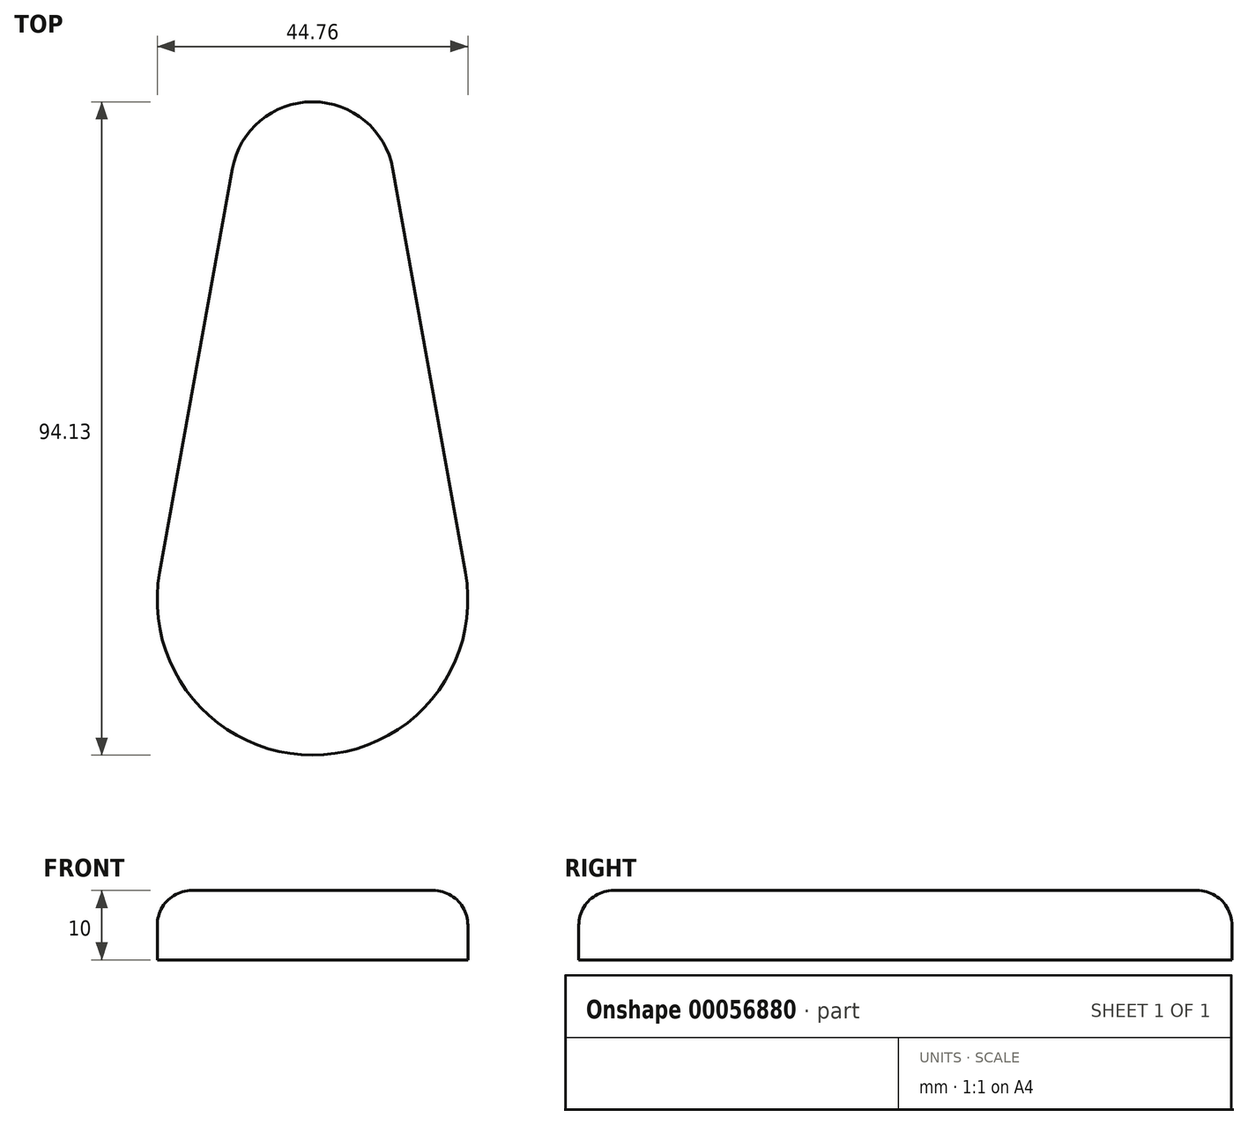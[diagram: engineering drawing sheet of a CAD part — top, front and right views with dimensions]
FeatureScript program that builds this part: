
annotation { "Feature Type Name" : "Feature", "Feature Type Description" : "" }
export const myFeature = defineFeature(function(context is Context, id is Id, definition is map)
    precondition{}
    {
        {
            var Q0;
            Q0=qCreatedBy(makeId("Top.planeOp"),FACE);
            var sketch = newSketch(context, id + "F0", { "sketchPlane" : qUnion([Q0])});
            skCircle(sketch, "E0", {"center": v(0, 0) * mm, "radius": 22.38 * mm});
            skCircle(sketch, "E1", {"center": v(0, 59.99) * mm, "radius": 11.76 * mm});
            skLineSegment(sketch, "E2", {"start": v(-11.57, 62.07) * mm, "end": v(-22.03, 3.96) * mm});
            skLineSegment(sketch, "E3", {"start": v(11.57, 62.07) * mm, "end": v(22.03, 3.96) * mm});
            skSolve(sketch);
        }
        {
            var Q0;
            {var subQ0=sQuery(id+"F0.wireOp",EDGE,"E0");var subQ1=makeQuery(id+"F0.imprint","INTERSECT",VERTEX,{"derivedFrom":[subQ0,sQuery(id+"F0.wireOp",EDGE,"E2")]});Q0=makeQuery(id+"F0.imprint","IMPRINT",FACE,{"disambiguationData":[TD([[makeQuery(id+"F0.imprint","IMPRINT",EDGE,{"disambiguationData":[TD([[subQ1,1.0]])],"derivedFrom":subQ0}),1.0]])]});}
            var Q1;
            {var subQ0=sQuery(id+"F0.wireOp",EDGE,"E2");Q1=makeQuery(id+"F0.imprint","IMPRINT",FACE,{"disambiguationData":[TD([[makeQuery(id+"F0.imprint","IMPRINT",EDGE,{"derivedFrom":subQ0}),1.0]])]});}
            var Q2;
            {var subQ0=sQuery(id+"F0.wireOp",EDGE,"E1");var subQ1=makeQuery(id+"F0.imprint","INTERSECT",VERTEX,{"derivedFrom":[subQ0,sQuery(id+"F0.wireOp",EDGE,"E2")]});Q2=makeQuery(id+"F0.imprint","IMPRINT",FACE,{"disambiguationData":[TD([[makeQuery(id+"F0.imprint","IMPRINT",EDGE,{"disambiguationData":[TD([[subQ1,1.0]])],"derivedFrom":subQ0}),1.0]])]});}
            extrude(context, id + "F1", {"entities" : qUnion([Q0, Q1, Q2]), "depth" : 10 * mm});
        }
        {
            var Q0;
            Q0=makeQuery(id+"F1.opExtrude","CAP_EDGE",EDGE,{"disambiguationData":[OSD([sQuery(id+"F0.wireOp",EDGE,"E0")])],"isStart":false});
            fillet(context, id + "F2", {"entities" : qUnion([Q0]), "radius" : 5 * mm, "tangentPropagation" : true, "allowEdgeOverflow" : false});
        }
    });
